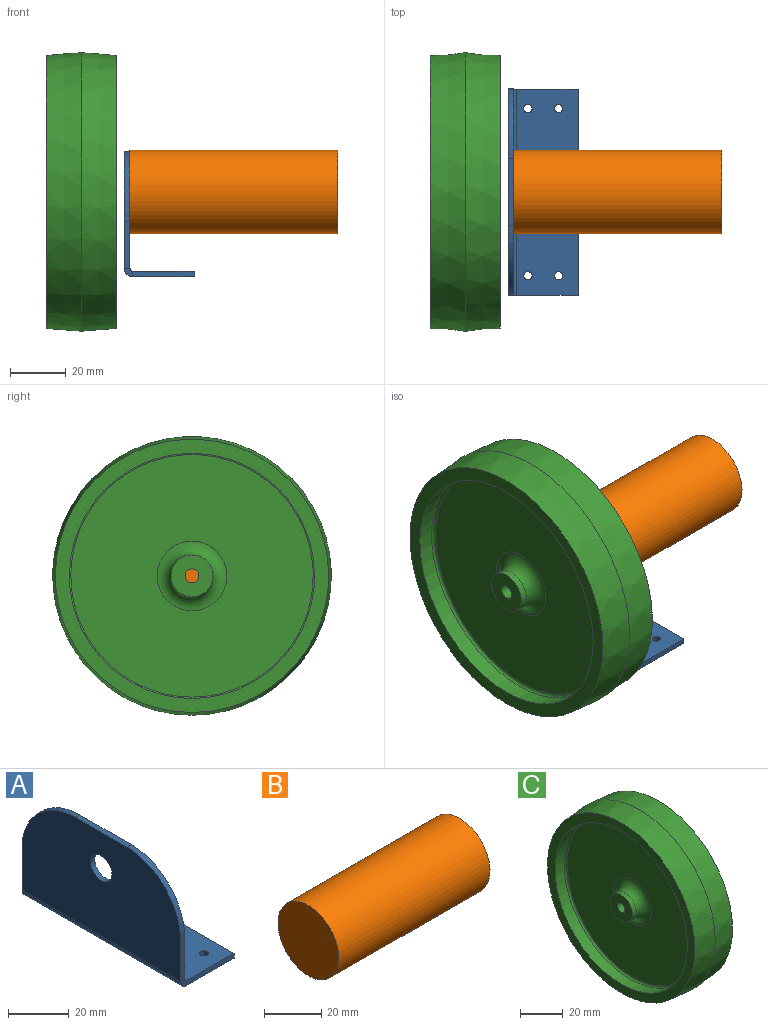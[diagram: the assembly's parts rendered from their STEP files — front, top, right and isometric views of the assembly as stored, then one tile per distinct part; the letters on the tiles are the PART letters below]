
ASSEMBLY  parts=3 mates=2
PART A: 21 faces, bbox 25x74x45 mm
  f0: plane 17x2mm, normal (0,1,0), area 34mm2, adj f5,f6,f7,f18
  f1: plane 17x2mm, normal (0,-1,0), area 34mm2, adj f2,f6,f7,f17
  f2: cylinder r=25mm len=25mm, axis (-1,0,0), area 78.5mm2, adj f1,f3,f6,f7
  f3: plane 24x2mm, normal (0,0,1), area 48mm2, adj f2,f5,f6,f7
  f4: cylinder r=5mm len=10mm, axis (-1,0,0), area 62.8mm2, adj f6,f7
  f5: cylinder r=25mm len=25mm, axis (-1,0,0), area 78.5mm2, adj f0,f3,f6,f7
  f6: plane 74x42mm, normal (-1,0,0), area 2761.2mm2, adj f0,f1,f2,f3,f4,f5,f19
  f7: plane 74x42mm, normal (1,0,0), area 2761.2mm2, adj f0,f1,f2,f3,f4,f5,f20
  f8: plane 22x2mm, normal (0,1,0), area 44mm2, adj f9,f15,f16,f18
  f9: plane 74x2mm, normal (1,0,0), area 148mm2, adj f8,f10,f15,f16
  f10: plane 22x2mm, normal (0,-1,0), area 44mm2, adj f9,f15,f16,f17
  f11: cylinder r=1.5mm len=3mm, axis (0,0,-1), area 18.8mm2, adj f15,f16
  f12: cylinder r=1.5mm len=3mm, axis (0,0,-1), area 18.8mm2, adj f15,f16
  f13: cylinder r=1.5mm len=3mm, axis (0,0,-1), area 18.8mm2, adj f15,f16
  f14: cylinder r=1.5mm len=3mm, axis (0,0,-1), area 18.8mm2, adj f15,f16
  f15: plane 74x22mm, normal (0,0,-1), area 1599.7mm2, adj f8,f9,f10,f11,f12,f13,f14,f19
  f16: plane 74x22mm, normal (0,0,1), area 1599.7mm2, adj f8,f9,f10,f11,f12,f13,f14,f20
  f17: plane 3x3mm, normal (0,-1,0), area 6.3mm2, adj f1,f10,f19,f20
  f18: plane 3x3mm, normal (0,1,0), area 6.3mm2, adj f0,f8,f19,f20
  f19: cylinder r=3mm len=74mm, axis (0,-1,0), area 348.7mm2, adj f6,f15,f17,f18
  f20: cylinder r=1mm len=74mm, axis (0,-1,0), area 116.2mm2, adj f7,f16,f17,f18
PART B: 3 faces, bbox 74.5x30x30 mm
  f0: cylinder r=15mm len=74.5mm, axis (-1,0,0), area 7021.5mm2, adj f1,f2
  f1: plane 30x30mm, normal (1,0,0), area 706.9mm2, adj f0
  f2: plane 30x30mm, normal (-1,0,0), area 706.9mm2, adj f0
PART C: 17 faces, bbox 27.1x100x100 mm
  f0: plane 15x15mm, normal (-1,0,0), area 157.1mm2, adj f3,f6
  f1: plane 98x98mm, normal (-1,0,0), area 1465.3mm2, adj f2,f5
  f2: cone r=50mm half-angle=4.6deg, axis (1,0,0), area 3900.1mm2, adj f1,f9
  f3: cylinder r=2.5mm len=25mm, axis (1,0,0), area 392.7mm2, adj f0,f7
  f4: plane 87x87mm, normal (-1,0,0), area 5454mm2, adj f14,f16
  f5: cone r=45.02mm half-angle=4.6deg, axis (1,0,0), area 1790.4mm2, adj f1,f16
  f6: cylinder r=7.5mm len=15mm, axis (1,0,0), area 117.8mm2, adj f0,f14
  f7: plane 15x15mm, normal (1,0,0), area 157.1mm2, adj f3,f12
  f8: plane 98x98mm, normal (1,0,0), area 1465.3mm2, adj f9,f11
  f9: cone r=50mm half-angle=4.6deg, axis (-1,0,0), area 3900.1mm2, adj f2,f8
  f10: plane 87x87mm, normal (1,0,0), area 5454mm2, adj f13,f15
  f11: cone r=45.02mm half-angle=4.6deg, axis (-1,0,0), area 1790.4mm2, adj f8,f15
  f12: cylinder r=7.5mm len=15mm, axis (-1,0,0), area 117.8mm2, adj f7,f13
  f13: torus R=12.5mm, axis (-1,0,0), area 459.8mm2, adj f10,f12
  f14: torus R=12.5mm, axis (1,0,0), area 459.8mm2, adj f4,f6
  f15: torus R=43.5mm, axis (-1,0,0), area 457.9mm2, adj f10,f11
  f16: torus R=43.5mm, axis (1,0,0), area 457.9mm2, adj f4,f5
PLACE A at identity fixed
PLACE B at identity
PLACE C at identity
MATE cylindrical B.f0 <-> A.f4  axis (-1,0,0) through (17.5,0,0)mm
MATE revolute C.f2 <-> A.f4  axis (-1,0,0) through (12.5,0,0)mm
